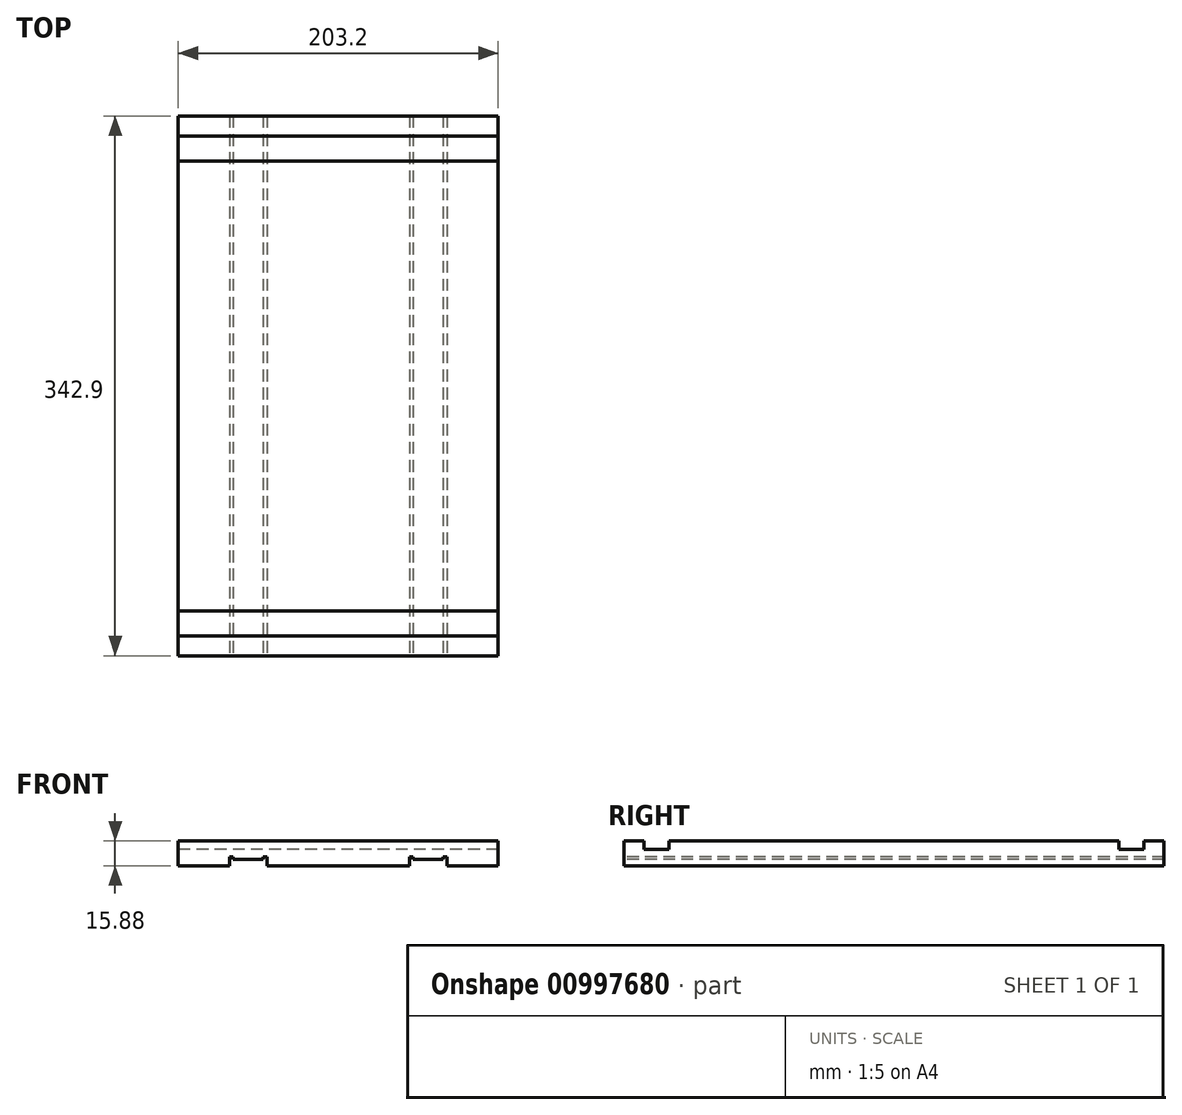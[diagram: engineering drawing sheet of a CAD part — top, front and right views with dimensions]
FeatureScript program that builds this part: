
annotation { "Feature Type Name" : "Feature", "Feature Type Description" : "" }
export const myFeature = defineFeature(function(context is Context, id is Id, definition is map)
    precondition{}
    {
        {
            var Q0;
            Q0=qCreatedBy(makeId("Front.planeOp"),FACE);
            var sketch = newSketch(context, id + "F0", { "sketchPlane" : qUnion([Q0])});
            skLineSegment(sketch, "E0", {"start": v(0, 15.87) * mm, "end": v(203.2, 15.87) * mm});
            skLineSegment(sketch, "E1", {"start": v(203.2, 15.87) * mm, "end": v(203.2, 0) * mm});
            skLineSegment(sketch, "E2", {"start": v(203.2, 0) * mm, "end": v(0, 0) * mm});
            skLineSegment(sketch, "E3", {"start": v(0, 0) * mm, "end": v(0, 15.87) * mm});
            skSolve(sketch);
        }
        {
            var Q0;
            Q0 = qSketchRegion(id + "F0", true);
            extrude(context, id + "F1", {"entities" : qUnion([Q0]), "depth" : 342.9 * mm, "offsetDistance" : 25.4 * mm});
        }
        {
            var Q0;
            Q0=makeQuery(id+"F1.opExtrude","CAP_FACE",FACE,{"disambiguationData":[OSD([sQuery(id+"F0.wireOp",EDGE,"E0"),sQuery(id+"F0.wireOp",EDGE,"E1"),sQuery(id+"F0.wireOp",EDGE,"E2"),sQuery(id+"F0.wireOp",EDGE,"E3")])],"isStart":false});
            var sketch = newSketch(context, id + "F2", { "sketchPlane" : qUnion([Q0])});
            skLineSegment(sketch, "E4", {"start": v(32.54, 0) * mm, "end": v(32.54, 5.56) * mm});
            skLineSegment(sketch, "E5", {"start": v(32.54, 5.56) * mm, "end": v(34.93, 5.56) * mm});
            skLineSegment(sketch, "E6", {"start": v(34.93, 5.56) * mm, "end": v(34.93, 3.97) * mm});
            skLineSegment(sketch, "E7", {"start": v(34.93, 3.97) * mm, "end": v(53.98, 3.97) * mm});
            skLineSegment(sketch, "E8", {"start": v(53.98, 3.97) * mm, "end": v(53.98, 5.56) * mm});
            skLineSegment(sketch, "E9", {"start": v(53.98, 5.56) * mm, "end": v(56.36, 5.56) * mm});
            skLineSegment(sketch, "E10", {"start": v(56.36, 5.56) * mm, "end": v(56.36, 0) * mm});
            skLineSegment(sketch, "E11", {"start": v(32.54, 0) * mm, "end": v(56.36, 0) * mm});
            skLineSegment(sketch, "E12", {"start": v(101.6, 15.87) * mm, "end": v(101.6, 0) * mm});
            skLineSegment(sketch, "E13.MirrorCS", {"start": v(168.28, 5.56) * mm, "end": v(168.28, 3.97) * mm});
            skLineSegment(sketch, "E14.MirrorCS", {"start": v(149.23, 3.97) * mm, "end": v(149.23, 5.56) * mm});
            skLineSegment(sketch, "E15.MirrorCS", {"start": v(170.66, 0) * mm, "end": v(146.84, 0) * mm});
            skLineSegment(sketch, "E16.MirrorCS", {"start": v(170.66, 5.56) * mm, "end": v(168.28, 5.56) * mm});
            skLineSegment(sketch, "E17.MirrorCS", {"start": v(170.66, 0) * mm, "end": v(170.66, 5.56) * mm});
            skLineSegment(sketch, "E18.MirrorCS", {"start": v(168.28, 3.97) * mm, "end": v(149.23, 3.97) * mm});
            skLineSegment(sketch, "E19.MirrorCS", {"start": v(146.84, 5.56) * mm, "end": v(146.84, 0) * mm});
            skLineSegment(sketch, "E20.MirrorCS", {"start": v(149.23, 5.56) * mm, "end": v(146.84, 5.56) * mm});
            skSolve(sketch);
        }
        {
            var Q0;
            Q0 = qSketchRegion(id + "F2", true);
            extrude(context, id + "F3", {"entities" : qUnion([Q0]), "operationType" : NewBodyOperationType.REMOVE, "endBound" : BoundingType.UP_TO_NEXT, "oppositeDirection" : true, "depth" : 25.4 * mm, "offsetDistance" : 25.4 * mm});
        }
        {
            var Q0;
            Q0=makeQuery(id+"F1.opExtrude","SWEPT_FACE",FACE,{"disambiguationData":[OSD([sQuery(id+"F0.wireOp",EDGE,"E3")])]});
            var sketch = newSketch(context, id + "F4", { "sketchPlane" : qUnion([Q0])});
            skLineSegment(sketch, "E21", {"start": v(12.7, 15.87) * mm, "end": v(12.7, 10.32) * mm});
            skLineSegment(sketch, "E22", {"start": v(12.7, 10.32) * mm, "end": v(28.58, 10.32) * mm});
            skLineSegment(sketch, "E23", {"start": v(28.58, 10.32) * mm, "end": v(28.58, 15.87) * mm});
            skLineSegment(sketch, "E24", {"start": v(28.58, 15.87) * mm, "end": v(12.7, 15.87) * mm});
            skLineSegment(sketch, "E25", {"start": v(171.45, 15.87) * mm, "end": v(171.45, 0) * mm, "construction": true});
            skLineSegment(sketch, "E26.MirrorCS", {"start": v(330.2, 15.87) * mm, "end": v(330.2, 10.32) * mm});
            skLineSegment(sketch, "E27.MirrorCS", {"start": v(330.2, 10.32) * mm, "end": v(314.33, 10.32) * mm});
            skLineSegment(sketch, "E28.MirrorCS", {"start": v(314.33, 15.87) * mm, "end": v(330.2, 15.87) * mm});
            skLineSegment(sketch, "E29.MirrorCS", {"start": v(314.33, 10.32) * mm, "end": v(314.33, 15.87) * mm});
            skSolve(sketch);
        }
        {
            var Q0;
            Q0 = qSketchRegion(id + "F4", true);
            extrude(context, id + "F5", {"entities" : qUnion([Q0]), "operationType" : NewBodyOperationType.REMOVE, "endBound" : BoundingType.UP_TO_NEXT, "oppositeDirection" : true, "depth" : 25.4 * mm, "offsetDistance" : 25.4 * mm});
        }
    });
